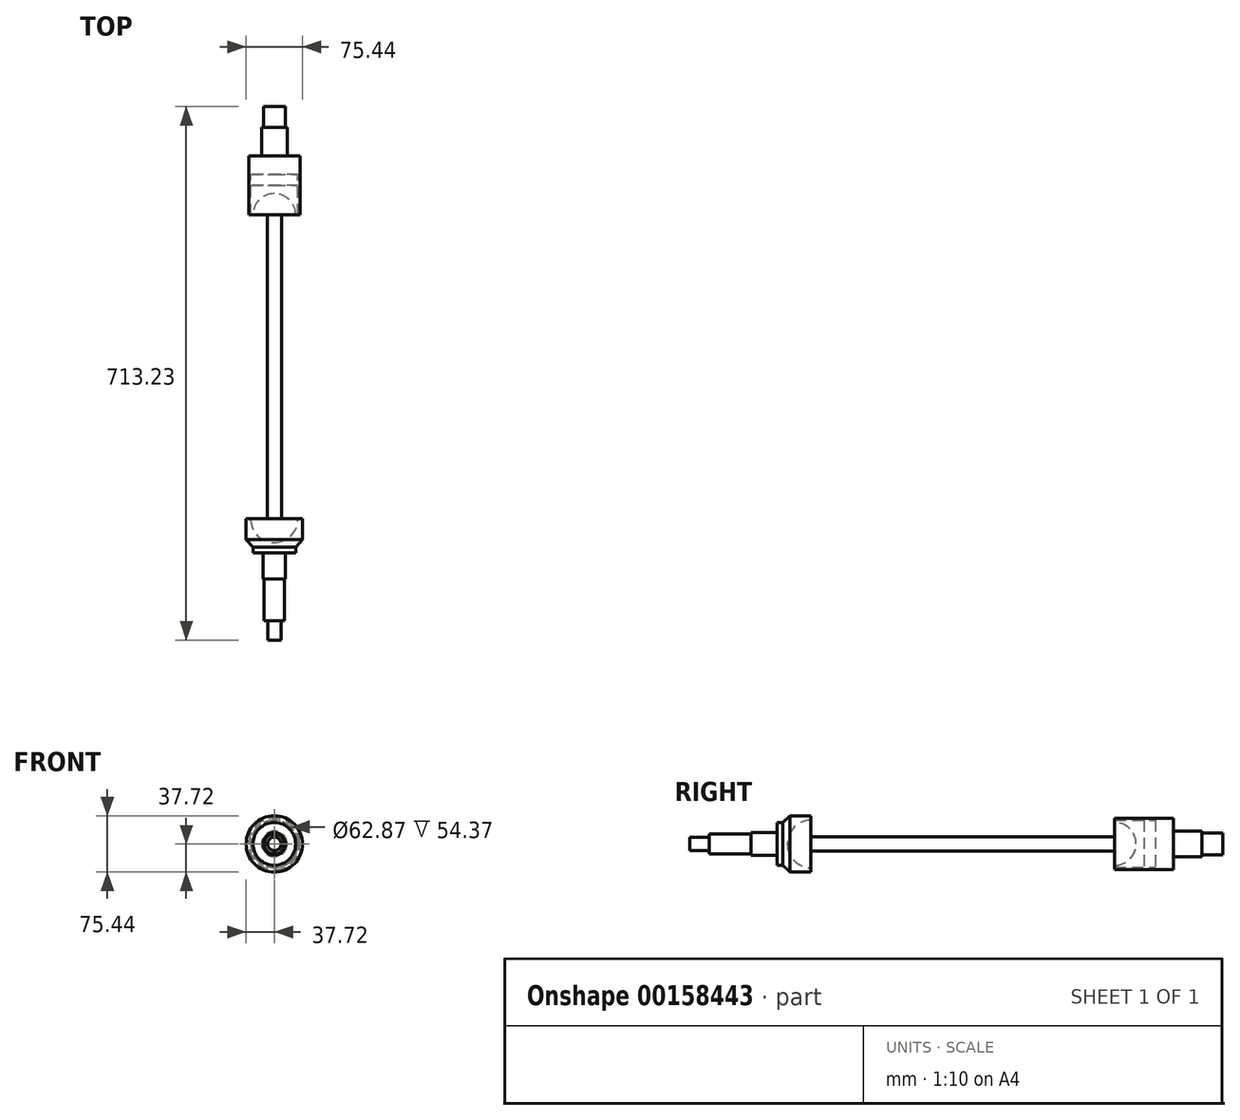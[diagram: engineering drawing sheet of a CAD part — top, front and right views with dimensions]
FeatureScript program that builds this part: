
annotation { "Feature Type Name" : "Feature", "Feature Type Description" : "" }
export const myFeature = defineFeature(function(context is Context, id is Id, definition is map)
    precondition{}
    {
        {
            var Q0;
            Q0=qCreatedBy(makeId("Right.planeOp"),FACE);
            var sketch = newSketch(context, id + "F0", { "sketchPlane" : qUnion([Q0])});
            skArc(sketch, "E0", {"start": v(217.49, 0) * mm, "mid": v(209.12, 20.2) * mm, "end": v(188.91, 28.58) * mm});
            skLineSegment(sketch, "E1", {"start": v(188.91, 28.58) * mm, "end": v(188.91, 9.52) * mm});
            skLineSegment(sketch, "E2", {"start": v(188.91, 9.53) * mm, "end": v(-217.49, 9.52) * mm});
            skLineSegment(sketch, "E3", {"start": v(217.49, 0) * mm, "end": v(-217.49, 0) * mm});
            skLineSegment(sketch, "E4", {"start": v(-217.49, 9.53) * mm, "end": v(-217.49, 31.75) * mm});
            skArc(sketch, "E5", {"start": v(-217.49, 31.75) * mm, "mid": v(-239.94, 22.45) * mm, "end": v(-249.24, 0) * mm});
            skLineSegment(sketch, "E6", {"start": v(-217.49, 0) * mm, "end": v(-249.24, 0) * mm});
            skSolve(sketch);
        }
        {
            var Q0;
            Q0=makeQuery(id+"F0.imprint","IMPRINT",FACE,{"disambiguationData":[TD([[makeQuery(id+"F0.imprint","IMPRINT",EDGE,{"derivedFrom":sQuery(id+"F0.wireOp",EDGE,"E0")}),1.0]])]});
            var Q1;
            Q1=sQuery(id+"F0.wireOp",EDGE,"E3");
            revolve(context, id + "F1", {"entities" : qUnion([Q0]), "axis" : qUnion([Q1]), "revolveType" : RevolveType.FULL});
        }
        {
            var Q0;
            Q0=qCreatedBy(makeId("Right.planeOp"),FACE);
            var sketch = newSketch(context, id + "F2", { "sketchPlane" : qUnion([Q0])});
            skLineSegment(sketch, "E7", {"start": v(-217.49, 37.72) * mm, "end": v(-245.43, 37.72) * mm});
            skLineSegment(sketch, "E8", {"start": v(-245.43, 37.72) * mm, "end": v(-255.46, 28.58) * mm});
            skLineSegment(sketch, "E9", {"start": v(-255.46, 28.58) * mm, "end": v(-263.08, 28.58) * mm});
            skLineSegment(sketch, "E10", {"start": v(-263.08, 28.58) * mm, "end": v(-263.08, 15.01) * mm});
            skLineSegment(sketch, "E11", {"start": v(-263.08, 15.01) * mm, "end": v(-298, 15.01) * mm});
            skLineSegment(sketch, "E12", {"start": v(-298, 15.01) * mm, "end": v(-298, 13.49) * mm});
            skLineSegment(sketch, "E13", {"start": v(-298, 13.49) * mm, "end": v(-353.89, 13.49) * mm});
            skLineSegment(sketch, "E14", {"start": v(-353.89, 13.49) * mm, "end": v(-353.89, 9) * mm});
            skLineSegment(sketch, "E15", {"start": v(-353.89, 9) * mm, "end": v(-379.54, 9) * mm});
            skLineSegment(sketch, "E16", {"start": v(-379.54, 9) * mm, "end": v(-379.54, 0) * mm});
            skLineSegment(sketch, "E17", {"start": v(-379.54, 0) * mm, "end": v(-249.24, 0) * mm});
            skLineSegment(sketch, "E18", {"start": v(-217.49, 31.75) * mm, "end": v(-217.49, 37.72) * mm});
            skArc(sketch, "E19", {"start": v(-217.49, 31.75) * mm, "mid": v(-239.94, 22.45) * mm, "end": v(-249.24, 0) * mm});
            skSolve(sketch);
        }
        {
            var Q0;
            Q0 = qSketchRegion(id + "F2", true);
            var Q1;
            Q1=sQuery(id+"F2.wireOp",EDGE,"E17");
            revolve(context, id + "F3", {"entities" : qUnion([Q0]), "axis" : qUnion([Q1]), "revolveType" : RevolveType.FULL});
        }
        {
            var Q0;
            Q0=qCreatedBy(makeId("Right.planeOp"),FACE);
            var sketch = newSketch(context, id + "F4", { "sketchPlane" : qUnion([Q0])});
            skLineSegment(sketch, "E20", {"start": v(188.91, 28.58) * mm, "end": v(188.91, 34.29) * mm});
            skLineSegment(sketch, "E21", {"start": v(188.91, 34.29) * mm, "end": v(267.65, 34.29) * mm});
            skLineSegment(sketch, "E22", {"start": v(267.65, 34.3) * mm, "end": v(267.65, 17.14) * mm});
            skLineSegment(sketch, "E23", {"start": v(267.65, 17.14) * mm, "end": v(305.75, 17.15) * mm});
            skLineSegment(sketch, "E24", {"start": v(305.75, 17.15) * mm, "end": v(305.75, 14.73) * mm});
            skLineSegment(sketch, "E25", {"start": v(305.75, 14.73) * mm, "end": v(333.7, 14.73) * mm});
            skLineSegment(sketch, "E26", {"start": v(333.7, 14.73) * mm, "end": v(333.7, 0) * mm});
            skLineSegment(sketch, "E27", {"start": v(333.7, 0) * mm, "end": v(217.49, 0) * mm});
            skArc(sketch, "E28", {"start": v(217.49, 0) * mm, "mid": v(209.12, 20.2) * mm, "end": v(188.91, 28.58) * mm});
            skLineSegment(sketch, "E29", {"start": v(188.91, 31.43) * mm, "end": v(228.28, 31.43) * mm});
            skPoint(sketch, "E29.endSnap0", {"position": v(228.28, 34.29) * mm});
            skLineSegment(sketch, "E30", {"start": v(228.28, 31.43) * mm, "end": v(228.28, 0) * mm});
            skLineSegment(sketch, "E31", {"start": v(228.28, 31.43) * mm, "end": v(243.28, 31.43) * mm});
            skLineSegment(sketch, "E32", {"start": v(243.28, 31.43) * mm, "end": v(243.28, 0) * mm});
            skSolve(sketch);
        }
        {
            var Q0;
            {var subQ1=sQuery(id+"F4.wireOp",EDGE,"E21");Q0=makeQuery(id+"F4.imprint","IMPRINT",FACE,{"disambiguationData":[TD([[makeQuery(id+"F4.imprint","IMPRINT",EDGE,{"derivedFrom":subQ1}),-1.0]])]});}
            var Q1;
            Q1=sQuery(id+"F4.wireOp",EDGE,"E27");
            revolve(context, id + "F5", {"entities" : qUnion([Q0]), "axis" : qUnion([Q1]), "revolveType" : RevolveType.FULL});
        }
        {
            var Q0;
            {var subQ1=sQuery(id+"F4.wireOp",EDGE,"E28");Q0=makeQuery(id+"F4.imprint","IMPRINT",FACE,{"disambiguationData":[TD([[makeQuery(id+"F4.imprint","IMPRINT",EDGE,{"derivedFrom":subQ1}),-1.0]])]});}
            var Q1;
            Q1=sQuery(id+"F4.wireOp",EDGE,"E27");
            revolve(context, id + "F6", {"entities" : qUnion([Q0]), "axis" : qUnion([Q1]), "revolveType" : RevolveType.FULL});
        }
    });
